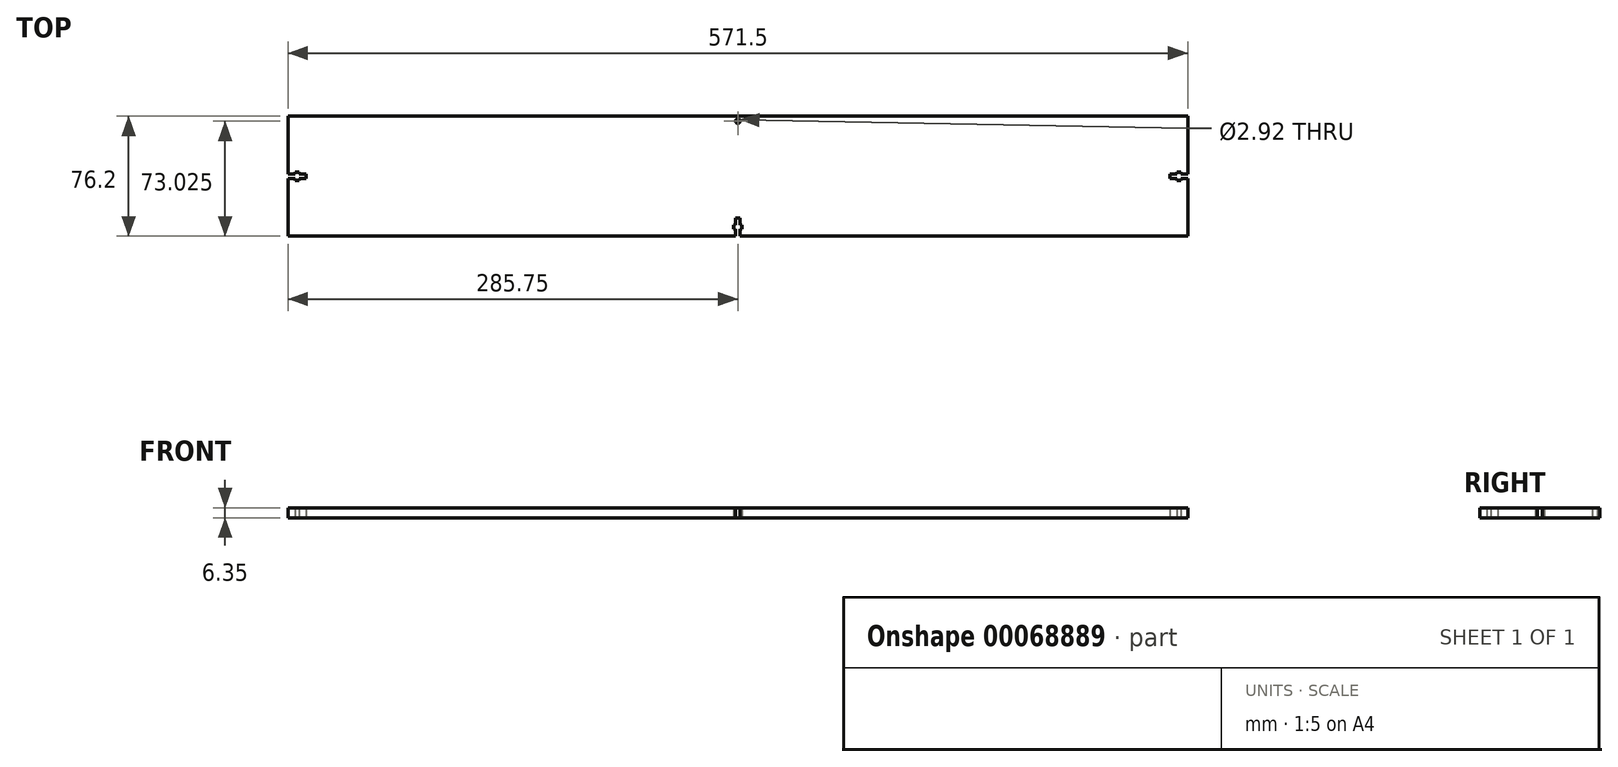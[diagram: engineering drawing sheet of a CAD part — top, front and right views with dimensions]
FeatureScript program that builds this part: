
annotation { "Feature Type Name" : "Feature", "Feature Type Description" : "" }
export const myFeature = defineFeature(function(context is Context, id is Id, definition is map)
    precondition{}
    {
        {
            var Q0;
            Q0=qCreatedBy(makeId("Top.planeOp"),FACE);
            var sketch = newSketch(context, id + "F0", { "sketchPlane" : qUnion([Q0])});
            skLineSegment(sketch, "E0.rect.bottom", {"start": v(285.75, -38.1) * mm, "end": v(1.46, -38.1) * mm});
            skLineSegment(sketch, "E0.rect.top", {"start": v(285.75, 38.1) * mm, "end": v(-285.75, 38.1) * mm});
            skLineSegment(sketch, "E0.rect.left", {"start": v(285.75, -38.1) * mm, "end": v(285.75, -1.46) * mm});
            skLineSegment(sketch, "E0.rect.right", {"start": v(-285.75, -38.1) * mm, "end": v(-285.75, -1.46) * mm});
            skPoint(sketch, "E0.rect.middle", {"position": v(0, 0) * mm});
            skLineSegment(sketch, "E1", {"start": v(0, 38.1) * mm, "end": v(0, -38.1) * mm, "construction": true});
            skLineSegment(sketch, "E2", {"start": v(-285.75, 0) * mm, "end": v(285.75, 0) * mm, "construction": true});
            skLineSegment(sketch, "E3.0", {"start": v(-1.46, 38.1) * mm, "end": v(-1.46, -38.1) * mm, "construction": true});
            skLineSegment(sketch, "E4", {"start": v(-1.46, -38.1) * mm, "end": v(-1.46, -33.66) * mm});
            skLineSegment(sketch, "E5", {"start": v(-1.46, -33.66) * mm, "end": v(-2.73, -33.66) * mm});
            skLineSegment(sketch, "E6", {"start": v(-2.73, -33.66) * mm, "end": v(-2.73, -31.12) * mm});
            skLineSegment(sketch, "E7", {"start": v(-2.73, -31.12) * mm, "end": v(-1.46, -31.12) * mm});
            skLineSegment(sketch, "E8", {"start": v(-1.46, -31.12) * mm, "end": v(-1.46, -26.67) * mm});
            skLineSegment(sketch, "E9", {"start": v(-1.46, -26.67) * mm, "end": v(0, -26.67) * mm});
            skLineSegment(sketch, "E10.MirrorCS", {"start": v(1.46, -26.67) * mm, "end": v(0, -26.67) * mm});
            skLineSegment(sketch, "E11.MirrorCS", {"start": v(1.46, -31.12) * mm, "end": v(1.46, -26.67) * mm});
            skLineSegment(sketch, "E12.MirrorCS", {"start": v(2.73, -31.12) * mm, "end": v(1.46, -31.12) * mm});
            skLineSegment(sketch, "E13.MirrorCS", {"start": v(2.73, -33.66) * mm, "end": v(2.73, -31.12) * mm});
            skLineSegment(sketch, "E14.MirrorCS", {"start": v(1.46, -33.66) * mm, "end": v(2.73, -33.66) * mm});
            skLineSegment(sketch, "E15.MirrorCS", {"start": v(1.46, -38.1) * mm, "end": v(1.46, -33.66) * mm});
            skLineSegment(sketch, "E16.trimOffspring", {"start": v(-1.46, -38.1) * mm, "end": v(-285.75, -38.1) * mm});
            skLineSegment(sketch, "E17.0", {"start": v(-285.75, -1.46) * mm, "end": v(298.45, -1.46) * mm, "construction": true});
            skLineSegment(sketch, "E18", {"start": v(-285.75, -1.46) * mm, "end": v(-281.3, -1.46) * mm});
            skLineSegment(sketch, "E19", {"start": v(-281.3, -1.46) * mm, "end": v(-281.3, -2.73) * mm});
            skLineSegment(sketch, "E20", {"start": v(-281.3, -2.73) * mm, "end": v(-278.77, -2.73) * mm});
            skLineSegment(sketch, "E21", {"start": v(-278.77, -2.73) * mm, "end": v(-278.77, -1.46) * mm});
            skLineSegment(sketch, "E22", {"start": v(-278.77, -1.46) * mm, "end": v(-274.32, -1.46) * mm});
            skLineSegment(sketch, "E23", {"start": v(-274.32, -1.46) * mm, "end": v(-274.32, 0) * mm});
            skLineSegment(sketch, "E24.MirrorCS", {"start": v(-274.32, 1.46) * mm, "end": v(-274.32, 0) * mm});
            skLineSegment(sketch, "E25.MirrorCS", {"start": v(-278.77, 1.46) * mm, "end": v(-274.32, 1.46) * mm});
            skLineSegment(sketch, "E26.MirrorCS", {"start": v(-278.77, 2.73) * mm, "end": v(-278.77, 1.46) * mm});
            skLineSegment(sketch, "E27.MirrorCS", {"start": v(-281.3, 2.73) * mm, "end": v(-278.77, 2.73) * mm});
            skLineSegment(sketch, "E28.MirrorCS", {"start": v(-281.3, 1.46) * mm, "end": v(-281.3, 2.73) * mm});
            skLineSegment(sketch, "E29.MirrorCS", {"start": v(-285.75, 1.46) * mm, "end": v(-281.3, 1.46) * mm});
            skLineSegment(sketch, "E30.MirrorCS", {"start": v(285.75, -1.46) * mm, "end": v(281.3, -1.46) * mm});
            skLineSegment(sketch, "E31.MirrorCS", {"start": v(281.3, -1.46) * mm, "end": v(281.3, -2.73) * mm});
            skLineSegment(sketch, "E32.MirrorCS", {"start": v(281.3, -2.73) * mm, "end": v(278.77, -2.73) * mm});
            skLineSegment(sketch, "E33.MirrorCS", {"start": v(278.77, -2.73) * mm, "end": v(278.77, -1.46) * mm});
            skLineSegment(sketch, "E34.MirrorCS", {"start": v(278.77, -1.46) * mm, "end": v(274.32, -1.46) * mm});
            skLineSegment(sketch, "E35.MirrorCS", {"start": v(274.32, -1.46) * mm, "end": v(274.32, 0) * mm});
            skLineSegment(sketch, "E36.MirrorCS", {"start": v(274.32, 1.46) * mm, "end": v(274.32, 0) * mm});
            skLineSegment(sketch, "E37.MirrorCS", {"start": v(278.77, 1.46) * mm, "end": v(274.32, 1.46) * mm});
            skLineSegment(sketch, "E38.MirrorCS", {"start": v(278.77, 2.73) * mm, "end": v(278.77, 1.46) * mm});
            skLineSegment(sketch, "E39.MirrorCS", {"start": v(281.3, 2.73) * mm, "end": v(278.77, 2.73) * mm});
            skLineSegment(sketch, "E40.MirrorCS", {"start": v(281.3, 1.46) * mm, "end": v(281.3, 2.73) * mm});
            skLineSegment(sketch, "E41.MirrorCS", {"start": v(285.75, 1.46) * mm, "end": v(281.3, 1.46) * mm});
            skLineSegment(sketch, "E42.trimOffspring", {"start": v(285.75, 1.46) * mm, "end": v(285.75, 38.1) * mm});
            skLineSegment(sketch, "E43.trimOffspring", {"start": v(-285.75, 1.46) * mm, "end": v(-285.75, 38.1) * mm});
            skLineSegment(sketch, "E44.0", {"start": v(311.15, 34.93) * mm, "end": v(-311.15, 34.92) * mm, "construction": true});
            skCircle(sketch, "E45", {"center": v(0, 34.92) * mm, "radius": 1.46 * mm});
            skSolve(sketch);
        }
        {
            var Q0;
            Q0=makeQuery(id+"F0.imprint","IMPRINT",FACE,{"disambiguationData":[TD([[makeQuery(id+"F0.imprint","IMPRINT",EDGE,{"derivedFrom":sQuery(id+"F0.wireOp",EDGE,"E0.rect.bottom")}),-1.0]])]});
            extrude(context, id + "F1", {"entities" : qUnion([Q0]), "depth" : 6.35 * mm});
        }
    });
